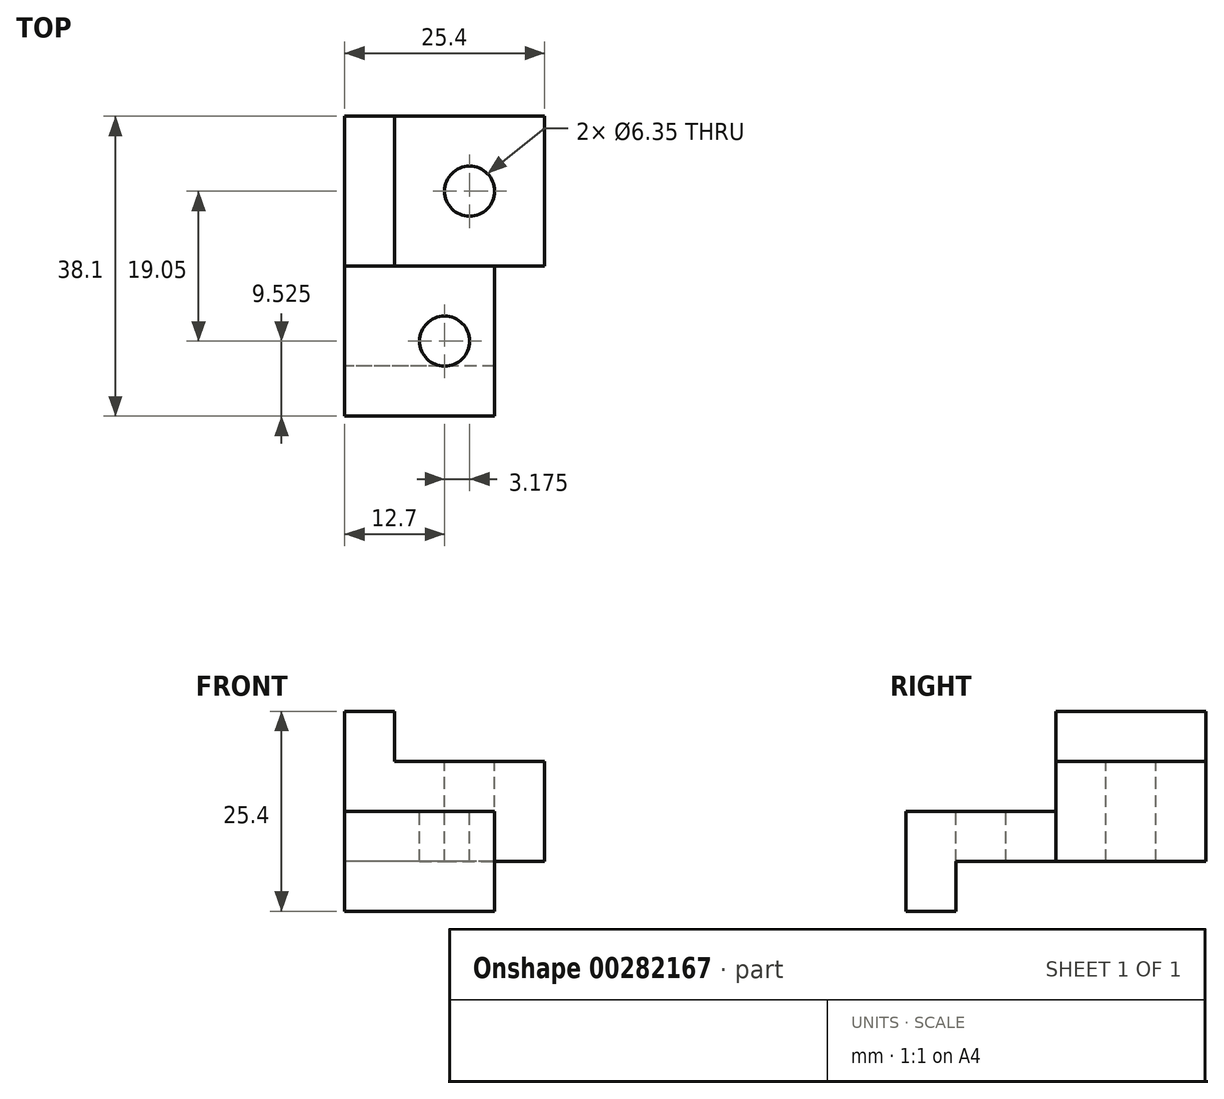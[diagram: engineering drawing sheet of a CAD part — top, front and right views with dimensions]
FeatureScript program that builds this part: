
annotation { "Feature Type Name" : "Feature", "Feature Type Description" : "" }
export const myFeature = defineFeature(function(context is Context, id is Id, definition is map)
    precondition{}
    {
        {
            var Q0;
            Q0=qCreatedBy(makeId("Right.planeOp"),FACE);
            var sketch = newSketch(context, id + "F0", { "sketchPlane" : qUnion([Q0])});
            skLineSegment(sketch, "E0", {"start": v(0, 0) * mm, "end": v(0, 12.7) * mm});
            skLineSegment(sketch, "E1", {"start": v(0, 12.7) * mm, "end": v(19.05, 12.7) * mm});
            skLineSegment(sketch, "E2", {"start": v(19.05, 12.7) * mm, "end": v(19.05, 25.4) * mm});
            skLineSegment(sketch, "E3", {"start": v(19.05, 25.4) * mm, "end": v(38.1, 25.4) * mm});
            skLineSegment(sketch, "E4", {"start": v(38.1, 25.4) * mm, "end": v(38.1, 6.35) * mm});
            skLineSegment(sketch, "E5", {"start": v(38.1, 6.35) * mm, "end": v(6.35, 6.35) * mm});
            skLineSegment(sketch, "E6", {"start": v(6.35, 6.35) * mm, "end": v(6.35, 0) * mm});
            skLineSegment(sketch, "E7", {"start": v(6.35, 0) * mm, "end": v(0, 0) * mm});
            skSolve(sketch);
        }
        {
            var Q0;
            Q0=makeQuery(id+"F0.imprint","IMPRINT",FACE,{"disambiguationData":[TD([[makeQuery(id+"F0.imprint","IMPRINT",EDGE,{"derivedFrom":sQuery(id+"F0.wireOp",EDGE,"E0")}),-1.0]])]});
            extrude(context, id + "F1", {"entities" : qUnion([Q0]), "depth" : 25.4 * mm});
        }
        {
            var Q0;
            Q0=makeQuery(id+"F1.opExtrude","SWEPT_FACE",FACE,{"disambiguationData":[OSD([sQuery(id+"F0.wireOp",EDGE,"E3")])]});
            var sketch = newSketch(context, id + "F2", { "sketchPlane" : qUnion([Q0])});
            skLineSegment(sketch, "E8.bottom", {"start": v(25.4, 38.1) * mm, "end": v(6.35, 38.1) * mm});
            skLineSegment(sketch, "E8.top", {"start": v(25.4, 19.05) * mm, "end": v(6.35, 19.05) * mm});
            skLineSegment(sketch, "E8.left", {"start": v(25.4, 38.1) * mm, "end": v(25.4, 19.05) * mm});
            skLineSegment(sketch, "E8.right", {"start": v(6.35, 38.1) * mm, "end": v(6.35, 19.05) * mm});
            skSolve(sketch);
        }
        {
            var Q0;
            Q0=makeQuery(id+"F2.imprint","IMPRINT",FACE,{"disambiguationData":[TD([[makeQuery(id+"F2.imprint","IMPRINT",EDGE,{"derivedFrom":sQuery(id+"F2.wireOp",EDGE,"E8.bottom")}),1.0]])]});
            extrude(context, id + "F3", {"entities" : qUnion([Q0]), "operationType" : NewBodyOperationType.REMOVE, "oppositeDirection" : true, "depth" : 6.35 * mm});
        }
        {
            var Q0;
            Q0=makeQuery(id+"F1.opExtrude","SWEPT_FACE",FACE,{"disambiguationData":[OSD([sQuery(id+"F0.wireOp",EDGE,"E1")])]});
            var sketch = newSketch(context, id + "F4", { "sketchPlane" : qUnion([Q0])});
            skCircle(sketch, "E9", {"center": v(12.7, 9.53) * mm, "radius": 3.18 * mm});
            skPoint(sketch, "E9.centerSnap0", {"position": v(25.4, 9.53) * mm});
            skPoint(sketch, "E9.centerSnap1", {"position": v(12.7, 0) * mm});
            skSolve(sketch);
        }
        {
            var Q0;
            Q0=makeQuery(id+"F4.imprint","IMPRINT",FACE,{"disambiguationData":[TD([[makeQuery(id+"F4.imprint","IMPRINT",EDGE,{"derivedFrom":sQuery(id+"F4.wireOp",EDGE,"E9")}),1.0]])]});
            extrude(context, id + "F5", {"entities" : qUnion([Q0]), "operationType" : NewBodyOperationType.REMOVE, "oppositeDirection" : true, "depth" : 6.35 * mm});
        }
        {
            var Q0;
            Q0=makeQuery(id+"F3.boolean.opBoolean","COPY",FACE,{"derivedFrom":makeQuery(id+"F3.opExtrude","CAP_FACE",FACE,{"disambiguationData":[OSD([sQuery(id+"F2.wireOp",EDGE,"E8.bottom"),sQuery(id+"F2.wireOp",EDGE,"E8.top"),sQuery(id+"F2.wireOp",EDGE,"E8.left"),sQuery(id+"F2.wireOp",EDGE,"E8.right")])],"isStart":false})});
            var sketch = newSketch(context, id + "F6", { "sketchPlane" : qUnion([Q0])});
            skCircle(sketch, "E10", {"center": v(15.88, 28.58) * mm, "radius": 3.18 * mm});
            skSolve(sketch);
        }
        {
            var Q0;
            Q0=makeQuery(id+"F6.imprint","IMPRINT",FACE,{"disambiguationData":[TD([[makeQuery(id+"F6.imprint","IMPRINT",EDGE,{"derivedFrom":sQuery(id+"F6.wireOp",EDGE,"E10")}),1.0]])]});
            extrude(context, id + "F7", {"entities" : qUnion([Q0]), "operationType" : NewBodyOperationType.REMOVE, "oppositeDirection" : true, "depth" : 19.05 * mm});
        }
        {
            var Q0;
            Q0=makeQuery(id+"F1.opExtrude","CAP_FACE",FACE,{"disambiguationData":[OSD([sQuery(id+"F0.wireOp",EDGE,"E0"),sQuery(id+"F0.wireOp",EDGE,"E1"),sQuery(id+"F0.wireOp",EDGE,"E2"),sQuery(id+"F0.wireOp",EDGE,"E3"),sQuery(id+"F0.wireOp",EDGE,"E4"),sQuery(id+"F0.wireOp",EDGE,"E5"),sQuery(id+"F0.wireOp",EDGE,"E6"),sQuery(id+"F0.wireOp",EDGE,"E7")])],"isStart":false});
            var sketch = newSketch(context, id + "F8", { "sketchPlane" : qUnion([Q0])});
            skLineSegment(sketch, "E11.bottom", {"start": v(0, 12.7) * mm, "end": v(19.05, 12.7) * mm});
            skLineSegment(sketch, "E11.right", {"start": v(19.05, 12.7) * mm, "end": v(19.05, 6.35) * mm});
            skLineSegment(sketch, "E12", {"start": v(0, 12.7) * mm, "end": v(0, 0) * mm});
            skLineSegment(sketch, "E13", {"start": v(0, 0) * mm, "end": v(6.35, 0) * mm});
            skLineSegment(sketch, "E14", {"start": v(6.35, 0) * mm, "end": v(6.35, 6.35) * mm});
            skLineSegment(sketch, "E15", {"start": v(6.35, 6.35) * mm, "end": v(19.05, 6.35) * mm});
            skSolve(sketch);
        }
        {
            var Q0;
            Q0=makeQuery(id+"F8.imprint","IMPRINT",FACE,{"disambiguationData":[TD([[makeQuery(id+"F8.imprint","IMPRINT",EDGE,{"derivedFrom":sQuery(id+"F8.wireOp",EDGE,"E11.bottom")}),-1.0]])]});
            extrude(context, id + "F9", {"entities" : qUnion([Q0]), "operationType" : NewBodyOperationType.REMOVE, "oppositeDirection" : true, "depth" : 6.35 * mm});
        }
    });
